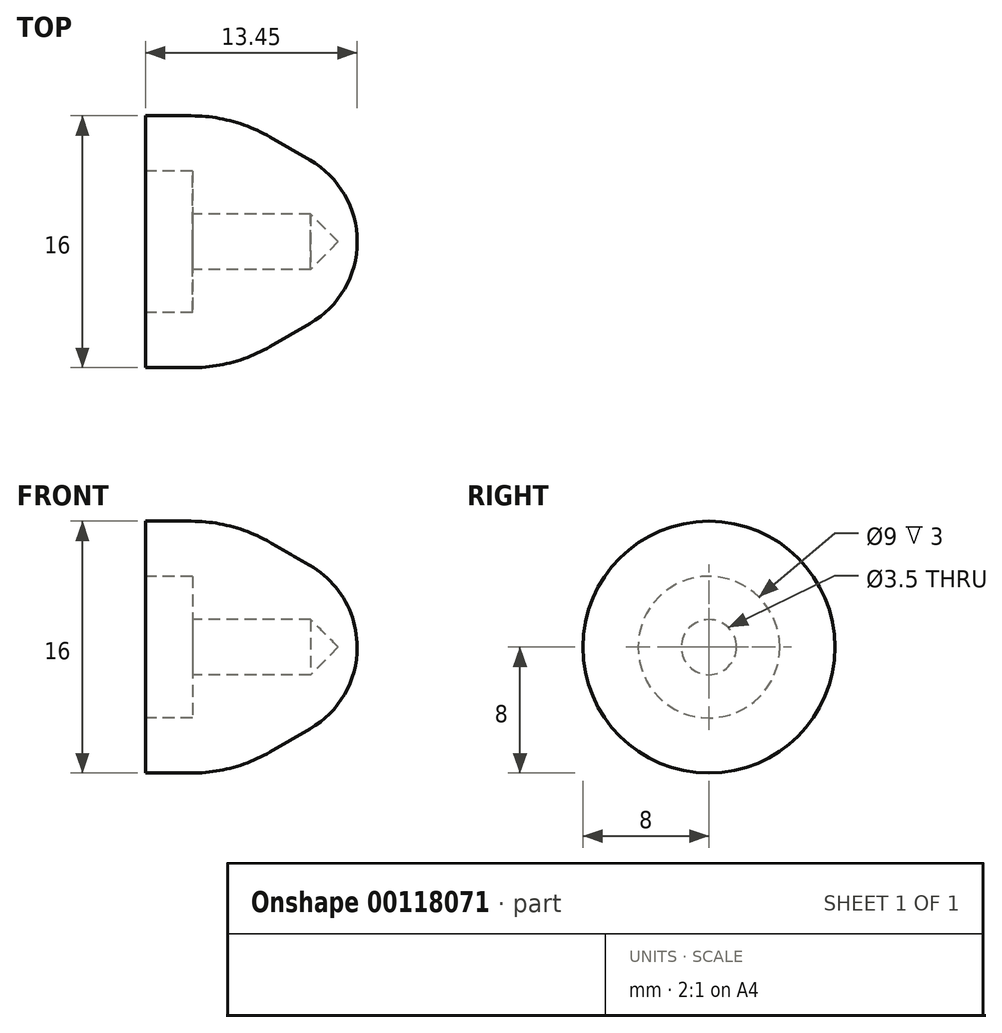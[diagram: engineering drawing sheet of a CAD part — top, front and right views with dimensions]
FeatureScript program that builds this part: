
annotation { "Feature Type Name" : "Feature", "Feature Type Description" : "" }
export const myFeature = defineFeature(function(context is Context, id is Id, definition is map)
    precondition{}
    {
        {
            var Q0;
            Q0=qCreatedBy(makeId("Front.planeOp"),FACE);
            var sketch = newSketch(context, id + "F0", { "sketchPlane" : qUnion([Q0])});
            skLineSegment(sketch, "E0", {"start": v(0, 1.75) * mm, "end": v(7.5, 1.75) * mm});
            skLineSegment(sketch, "E1", {"start": v(7.5, 1.75) * mm, "end": v(9.25, 0) * mm});
            skLineSegment(sketch, "E2", {"start": v(0, 1.75) * mm, "end": v(0, 4.5) * mm});
            skLineSegment(sketch, "E3", {"start": v(0, 4.5) * mm, "end": v(-3, 4.5) * mm});
            skLineSegment(sketch, "E4", {"start": v(-3, 4.5) * mm, "end": v(-3, 8) * mm});
            skArc(sketch, "E5", {"start": v(10.45, 0) * mm, "mid": v(9.65, 3) * mm, "end": v(7.45, 5.2) * mm});
            skLineSegment(sketch, "E6", {"start": v(7.45, 5.2) * mm, "end": v(4.91, 6.66) * mm});
            skLineSegment(sketch, "E7", {"start": v(-0.09, 8) * mm, "end": v(-3, 8) * mm});
            skPoint(sketch, "E8.visualSharp", {"position": v(2.6, 8) * mm});
            skArc(sketch, "E8.filletArc", {"start": v(4.91, 6.66) * mm, "mid": v(2.5, 7.66) * mm, "end": v(-0.09, 8) * mm});
            skLineSegment(sketch, "E9", {"start": v(0, 0) * mm, "end": v(4.26, 0) * mm});
            skLineSegment(sketch, "E10", {"start": v(9.25, 0) * mm, "end": v(10.45, 0) * mm});
            skSolve(sketch);
        }
        {
            var Q0;
            Q0=makeQuery(id+"F0.imprint","IMPRINT",FACE,{"disambiguationData":[TD([[makeQuery(id+"F0.imprint","IMPRINT",EDGE,{"derivedFrom":sQuery(id+"F0.wireOp",EDGE,"E0")}),1.0]])]});
            var Q1;
            Q1=sQuery(id+"F0.wireOp",EDGE,"E10");
            revolve(context, id + "F1", {"entities" : qUnion([Q0]), "axis" : qUnion([Q1]), "revolveType" : RevolveType.FULL});
        }
    });
